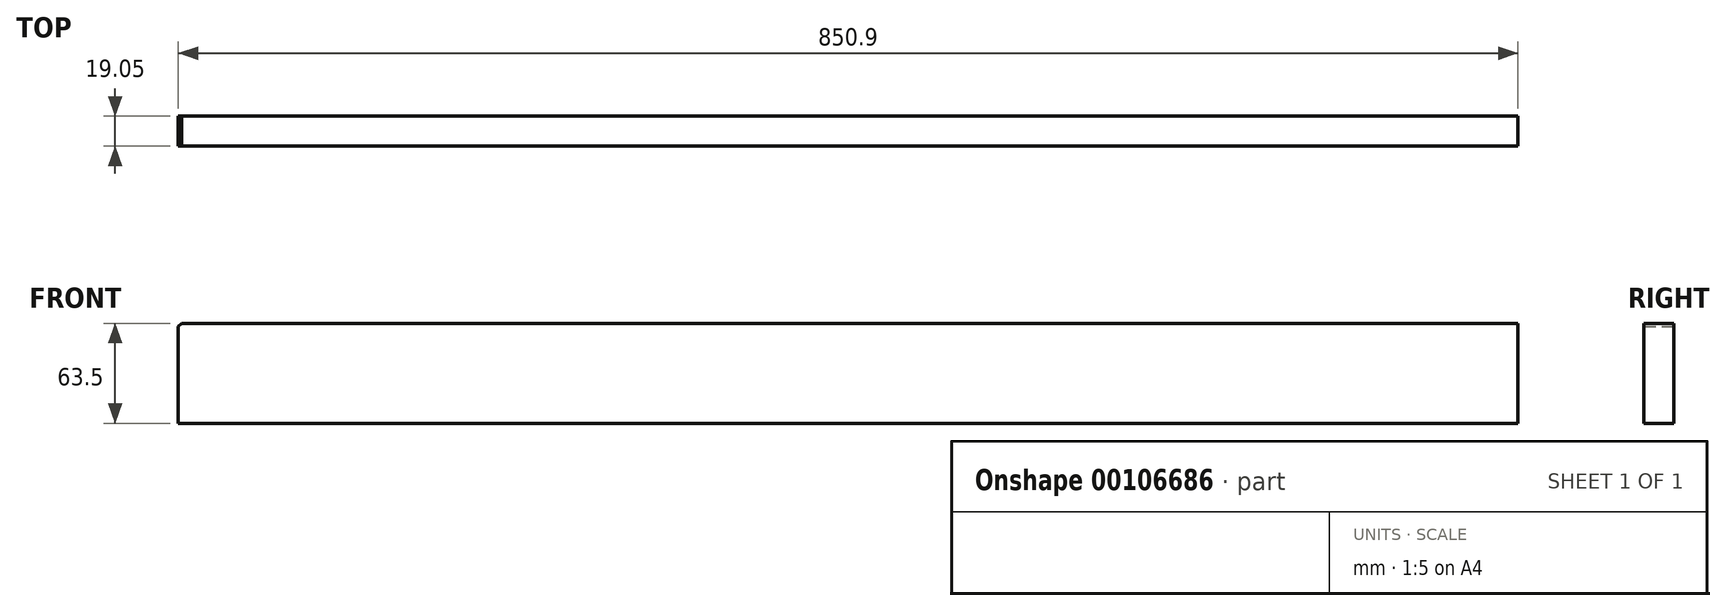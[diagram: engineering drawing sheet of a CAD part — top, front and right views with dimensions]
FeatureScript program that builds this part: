
annotation { "Feature Type Name" : "Feature", "Feature Type Description" : "" }
export const myFeature = defineFeature(function(context is Context, id is Id, definition is map)
    precondition{}
    {
        {
            var Q0;
            Q0=qCreatedBy(makeId("Front.planeOp"),FACE);
            var sketch = newSketch(context, id + "F0", { "sketchPlane" : qUnion([Q0])});
            skLineSegment(sketch, "E0.bottom", {"start": v(63.5, 0) * mm, "end": v(914.4, 0) * mm});
            skLineSegment(sketch, "E0.top", {"start": v(65.55, 63.5) * mm, "end": v(914.4, 63.5) * mm});
            skLineSegment(sketch, "E0.right", {"start": v(914.4, 0) * mm, "end": v(914.4, 63.5) * mm});
            skLineSegment(sketch, "E1", {"start": v(63.5, 61.52) * mm, "end": v(65.55, 63.5) * mm});
            skLineSegment(sketch, "E2", {"start": v(63.5, 61.52) * mm, "end": v(63.5, 0) * mm});
            skPoint(sketch, "E3.orphan", {"position": v(0, 0) * mm});
            skSolve(sketch);
        }
        {
            var Q0;
            Q0=makeQuery(id+"F0.imprint","IMPRINT",FACE,{"disambiguationData":[TD([[makeQuery(id+"F0.imprint","IMPRINT",EDGE,{"derivedFrom":sQuery(id+"F0.wireOp",EDGE,"E0.bottom")}),1.0]])]});
            extrude(context, id + "F1", {"entities" : qUnion([Q0]), "depth" : 19.05 * mm});
        }
    });
